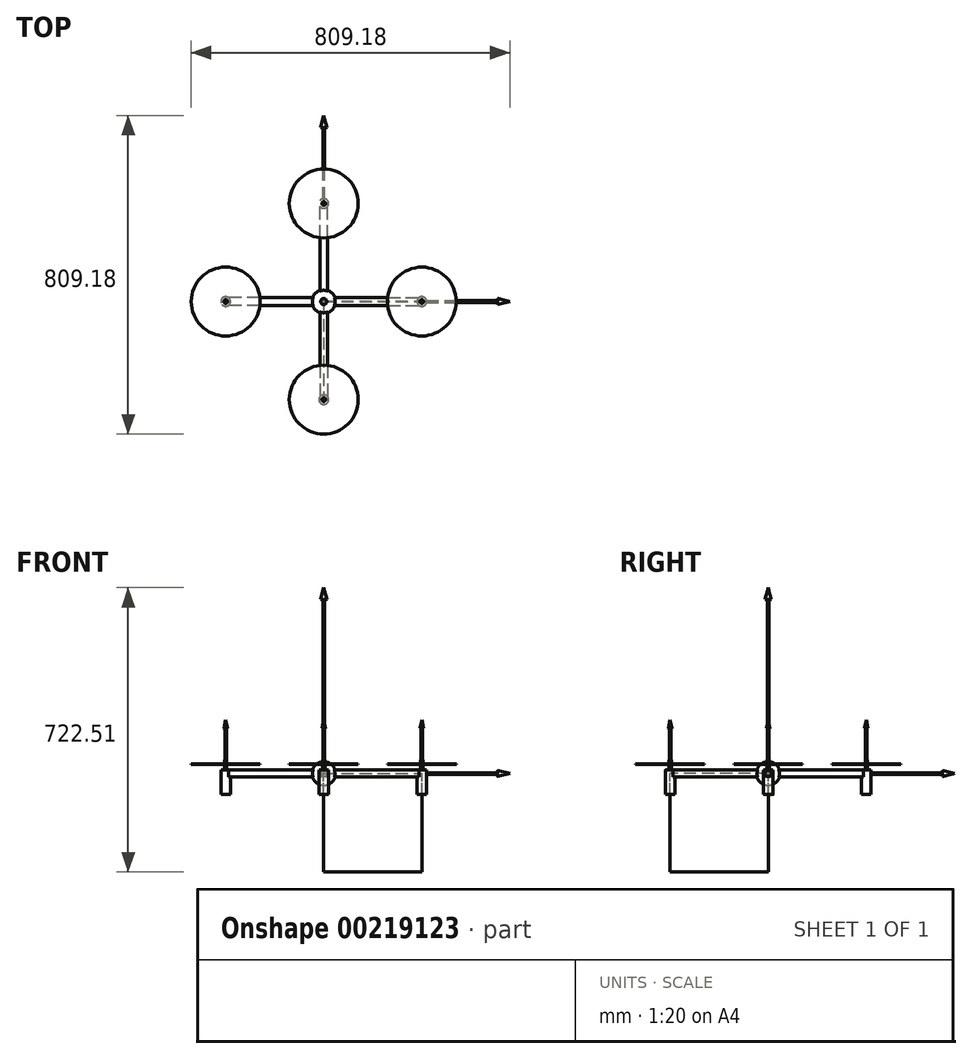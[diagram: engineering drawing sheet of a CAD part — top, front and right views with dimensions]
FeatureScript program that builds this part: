
annotation { "Feature Type Name" : "Feature", "Feature Type Description" : "" }
export const myFeature = defineFeature(function(context is Context, id is Id, definition is map)
    precondition{}
    {
        {
            var Q0;
            Q0=qCreatedBy(makeId("Top.planeOp"),FACE);
            var sketch = newSketch(context, id + "F0", { "sketchPlane" : qUnion([Q0])});
            skLineSegment(sketch, "E0.bottom", {"start": v(0, 0) * mm, "end": v(-10, 0) * mm});
            skLineSegment(sketch, "E0.top", {"start": v(7.68, 250) * mm, "end": v(-10, 250) * mm});
            skLineSegment(sketch, "E0.right", {"start": v(-10, 0) * mm, "end": v(-10, 250) * mm});
            skLineSegment(sketch, "E1.MirrorCS", {"start": v(-7.68, 250) * mm, "end": v(10, 250) * mm});
            skLineSegment(sketch, "E2.MirrorCS", {"start": v(0, 0) * mm, "end": v(10, 0) * mm});
            skLineSegment(sketch, "E3.MirrorCS", {"start": v(10, 0) * mm, "end": v(10, 250) * mm});
            skLineSegment(sketch, "E4.1.0", {"start": v(0.03, 10) * mm, "end": v(-249.97, 10) * mm});
            skLineSegment(sketch, "E4.1.1", {"start": v(0.03, -10) * mm, "end": v(-249.97, -10) * mm});
            skLineSegment(sketch, "E4.1.2", {"start": v(0.03, 0) * mm, "end": v(0.03, 10) * mm});
            skLineSegment(sketch, "E4.1.3", {"start": v(-249.97, 7.68) * mm, "end": v(-249.97, -10) * mm});
            skLineSegment(sketch, "E4.1.4", {"start": v(-249.97, -7.68) * mm, "end": v(-249.97, 10) * mm});
            skLineSegment(sketch, "E4.1.5", {"start": v(0.03, 0) * mm, "end": v(0.03, -10) * mm});
            skLineSegment(sketch, "E4.2.0", {"start": v(-9.97, 0.03) * mm, "end": v(-9.97, -249.97) * mm});
            skLineSegment(sketch, "E4.2.1", {"start": v(10.03, 0.03) * mm, "end": v(10.03, -249.97) * mm});
            skLineSegment(sketch, "E4.2.2", {"start": v(0.03, 0.03) * mm, "end": v(-9.97, 0.03) * mm});
            skLineSegment(sketch, "E4.2.3", {"start": v(-7.65, -249.97) * mm, "end": v(10.03, -249.97) * mm});
            skLineSegment(sketch, "E4.2.4", {"start": v(7.71, -249.97) * mm, "end": v(-9.97, -249.97) * mm});
            skLineSegment(sketch, "E4.2.5", {"start": v(0.03, 0.03) * mm, "end": v(10.03, 0.03) * mm});
            skLineSegment(sketch, "E4.3.0", {"start": v(0, -9.97) * mm, "end": v(250, -9.97) * mm});
            skLineSegment(sketch, "E4.3.1", {"start": v(0, 10.03) * mm, "end": v(250, 10.03) * mm});
            skLineSegment(sketch, "E4.3.2", {"start": v(0, 0.03) * mm, "end": v(0, -9.97) * mm});
            skLineSegment(sketch, "E4.3.3", {"start": v(250, -7.65) * mm, "end": v(250, 10.03) * mm});
            skLineSegment(sketch, "E4.3.4", {"start": v(250, 7.71) * mm, "end": v(250, -9.97) * mm});
            skLineSegment(sketch, "E4.3.5", {"start": v(0, 0.03) * mm, "end": v(0, 10.03) * mm});
            skPoint(sketch, "E4.center", {"position": v(0.01, 0.01) * mm});
            skCircle(sketch, "E5", {"center": v(0, 250) * mm, "radius": 10.03 * mm});
            skPoint(sketch, "E5.centerSnap0", {"position": v(1.16, 250) * mm});
            skSolve(sketch);
        }
        {
            var Q0;
            Q0 = qSketchRegion(id + "F0", true);
            extrude(context, id + "F1", {"entities" : qUnion([Q0]), "endBound" : BoundingType.SYMMETRIC, "depth" : 18 * mm});
        }
        {
            var Q0;
            Q0=qCreatedBy(makeId("Top.planeOp"),FACE);
            var sketch = newSketch(context, id + "F2", { "sketchPlane" : qUnion([Q0])});
            skArc(sketch, "E6", {"start": v(30, 0) * mm, "mid": v(0, 30) * mm, "end": v(-30, 0) * mm});
            skLineSegment(sketch, "E7", {"start": v(0, 0) * mm, "end": v(309.13, 0) * mm, "construction": true});
            skLineSegment(sketch, "E8", {"start": v(0, 0) * mm, "end": v(30, 0) * mm});
            skLineSegment(sketch, "E9", {"start": v(-30, 0) * mm, "end": v(0, 0) * mm});
            skLineSegment(sketch, "E10", {"start": v(0, 320.77) * mm, "end": v(0, 0) * mm, "construction": true});
            skSolve(sketch);
        }
        {
            var Q0;
            Q0=makeQuery(id+"F2.imprint","IMPRINT",FACE,{"disambiguationData":[TD([[makeQuery(id+"F2.imprint","IMPRINT",EDGE,{"derivedFrom":sQuery(id+"F2.wireOp",EDGE,"E6")}),1.0]])]});
            var Q1;
            Q1=sQuery(id+"F2.wireOp",EDGE,"E7");
            revolve(context, id + "F3", {"operationType" : NewBodyOperationType.ADD, "entities" : qUnion([Q0]), "axis" : qUnion([Q1]), "revolveType" : RevolveType.FULL});
        }
        {
            var Q0;
            Q0=makeQuery(id+"F1.opExtrude","CAP_FACE",FACE,{"disambiguationData":[OSD([sQuery(id+"F0.wireOp",EDGE,"E0.bottom"),sQuery(id+"F0.wireOp",EDGE,"E0.right"),sQuery(id+"F0.wireOp",EDGE,"E2.MirrorCS"),sQuery(id+"F0.wireOp",EDGE,"E3.MirrorCS"),sQuery(id+"F0.wireOp",EDGE,"E4.1.0"),sQuery(id+"F0.wireOp",EDGE,"E4.1.1"),sQuery(id+"F0.wireOp",EDGE,"E4.1.2"),sQuery(id+"F0.wireOp",EDGE,"E4.1.3"),sQuery(id+"F0.wireOp",EDGE,"E4.1.4"),sQuery(id+"F0.wireOp",EDGE,"E4.1.5"),sQuery(id+"F0.wireOp",EDGE,"E4.2.0"),sQuery(id+"F0.wireOp",EDGE,"E4.2.1"),sQuery(id+"F0.wireOp",EDGE,"E4.2.2"),sQuery(id+"F0.wireOp",EDGE,"E4.2.3"),sQuery(id+"F0.wireOp",EDGE,"E4.2.4"),sQuery(id+"F0.wireOp",EDGE,"E4.2.5"),sQuery(id+"F0.wireOp",EDGE,"E4.3.0"),sQuery(id+"F0.wireOp",EDGE,"E4.3.1"),sQuery(id+"F0.wireOp",EDGE,"E4.3.2"),sQuery(id+"F0.wireOp",EDGE,"E4.3.3"),sQuery(id+"F0.wireOp",EDGE,"E4.3.4"),sQuery(id+"F0.wireOp",EDGE,"E4.3.5"),sQuery(id+"F0.wireOp",EDGE,"E5")])],"isStart":false});
            var sketch = newSketch(context, id + "F4", { "sketchPlane" : qUnion([Q0])});
            skCircle(sketch, "E11", {"center": v(0, 249.17) * mm, "radius": 12.17 * mm});
            skCircle(sketch, "E12.1.0", {"center": v(-249.17, 0) * mm, "radius": 12.17 * mm});
            skCircle(sketch, "E12.2.0", {"center": v(0, -249.17) * mm, "radius": 12.17 * mm});
            skCircle(sketch, "E12.3.0", {"center": v(249.17, 0) * mm, "radius": 12.17 * mm});
            skPoint(sketch, "E12.center", {"position": v(0, 0) * mm});
            skSolve(sketch);
        }
        {
            var Q0;
            Q0 = qSketchRegion(id + "F4", true);
            extrude(context, id + "F5", {"entities" : qUnion([Q0]), "operationType" : NewBodyOperationType.ADD, "oppositeDirection" : true, "depth" : 62.5 * mm});
        }
        {
            var Q0;
            Q0=qCreatedBy(makeId("Front.planeOp"),FACE);
            var sketch = newSketch(context, id + "F6", { "sketchPlane" : qUnion([Q0])});
            skLineSegment(sketch, "E13", {"start": v(0, 0) * mm, "end": v(0, 184.57) * mm, "construction": true});
            skSolve(sketch);
        }
        {
            var Q0;
            Q0=qCreatedBy(makeId("Top.planeOp"),FACE);
            var sketch = newSketch(context, id + "F7", { "sketchPlane" : qUnion([Q0])});
            skLineSegment(sketch, "E14.0", {"start": v(-2, 441.97) * mm, "end": v(-2, 0) * mm});
            skLineSegment(sketch, "E15", {"start": v(0, 441.97) * mm, "end": v(0, 0) * mm});
            skLineSegment(sketch, "E16", {"start": v(0, 0) * mm, "end": v(-2, 0) * mm});
            skPoint(sketch, "E17.center", {"position": v(0, 0) * mm});
            skLineSegment(sketch, "E18", {"start": v(-2, 0) * mm, "end": v(0, 0) * mm});
            skLineSegment(sketch, "E19.1.0", {"start": v(441.97, 2) * mm, "end": v(441.97, 0) * mm});
            skLineSegment(sketch, "E19.1.1", {"start": v(441.97, 2) * mm, "end": v(0, 2) * mm});
            skLineSegment(sketch, "E19.1.2", {"start": v(441.97, 0) * mm, "end": v(0, 0) * mm});
            skLineSegment(sketch, "E19.1.3", {"start": v(0, 2) * mm, "end": v(0, 0) * mm});
            skLineSegment(sketch, "E20", {"start": v(-2, 441.97) * mm, "end": v(-7.85, 441.97) * mm});
            skLineSegment(sketch, "E21", {"start": v(0, 472.51) * mm, "end": v(-7.85, 441.97) * mm});
            skLineSegment(sketch, "E22", {"start": v(0, 472.51) * mm, "end": v(0, 441.97) * mm});
            skSolve(sketch);
        }
        {
            var Q0;
            Q0=makeQuery(id+"F7.imprint","IMPRINT",FACE,{"disambiguationData":[TD([[makeQuery(id+"F7.imprint","IMPRINT",EDGE,{"derivedFrom":sQuery(id+"F7.wireOp",EDGE,"E15")}),-1.0]])]});
            var Q1;
            {var subQ3=sQuery(id+"F7.wireOp",EDGE,"E21");Q1=makeQuery(id+"F7.imprint","IMPRINT",FACE,{"disambiguationData":[TD([[makeQuery(id+"F7.imprint","IMPRINT",EDGE,{"derivedFrom":subQ3}),-1.0]])]});}
            var Q2;
            Q2=sQuery(id+"F7.wireOp",EDGE,"E15");
            revolve(context, id + "F8", {"entities" : qUnion([Q0, Q1]), "axis" : qUnion([Q2]), "revolveType" : RevolveType.FULL});
        }
        {
            var Q0;
            Q0=makeQuery(id+"F8.opRevolve","SWEPT_BODY",BODY,{"disambiguationData":[OSD([sQuery(id+"F7.wireOp",EDGE,"E15"),sQuery(id+"F7.wireOp",EDGE,"E14.0"),sQuery(id+"F7.wireOp",EDGE,"phnClhmD-Ye00-Ug2d-337D-V6CSu4RFdTta"),sQuery(id+"F7.wireOp",EDGE,"E18")])]});
            var Q1;
            Q1=sQuery(id+"F2.wireOp",EDGE,"E8");
            circularPattern(context, id + "F9", {"entities" : qUnion([Q0]), "axis" : qUnion([Q1]), "angle" : 90 * degree, "instanceCount" : 2, "equalSpace" : true});
        }
        {
            var Q0;
            Q0=makeQuery(id+"F9.opPattern","COPY",BODY,{"derivedFrom":makeQuery(id+"F8.opRevolve","SWEPT_BODY",BODY,{"disambiguationData":[OSD([sQuery(id+"F7.wireOp",EDGE,"E15"),sQuery(id+"F7.wireOp",EDGE,"E14.0"),sQuery(id+"F7.wireOp",EDGE,"phnClhmD-Ye00-Ug2d-337D-V6CSu4RFdTta"),sQuery(id+"F7.wireOp",EDGE,"E18"),sQuery(id+"F7.wireOp",EDGE,"E19.1.3")])]}),"instanceName":"1"});
            var Q1;
            Q1=sQuery(id+"F2.wireOp",EDGE,"E10");
            circularPattern(context, id + "F10", {"operationType" : NewBodyOperationType.ADD, "entities" : qUnion([Q0]), "axis" : qUnion([Q1]), "angle" : 270 * degree, "instanceCount" : 2, "equalSpace" : true});
        }
        {
            var Q0;
            {var subQ0=sQuery(id+"F0.wireOp",EDGE,"E0.right");var subQ1=sQuery(id+"F0.wireOp",EDGE,"E4.3.1");var subQ2=sQuery(id+"F0.wireOp",EDGE,"E3.MirrorCS");var subQ3=sQuery(id+"F0.wireOp",EDGE,"E5");Q0=makeQuery(id+"F5.boolean.opBoolean","MERGE",FACE,{"derivedFrom":[makeQuery(id+"F3.boolean.opBoolean","SPLIT",FACE,{"disambiguationData":[TD([makeQuery(id+"F1.opExtrude","SWEPT_FACE",FACE,{"disambiguationData":[OSD([subQ0])]})])],"derivedFrom":makeQuery(id+"F1.opExtrude","CAP_FACE",FACE,{"disambiguationData":[OSD([sQuery(id+"F0.wireOp",EDGE,"E0.bottom"),subQ0,sQuery(id+"F0.wireOp",EDGE,"E2.MirrorCS"),subQ2,sQuery(id+"F0.wireOp",EDGE,"E4.1.0"),sQuery(id+"F0.wireOp",EDGE,"E4.1.1"),sQuery(id+"F0.wireOp",EDGE,"E4.1.2"),sQuery(id+"F0.wireOp",EDGE,"E4.1.3"),sQuery(id+"F0.wireOp",EDGE,"E4.1.4"),sQuery(id+"F0.wireOp",EDGE,"E4.1.5"),sQuery(id+"F0.wireOp",EDGE,"E4.2.0"),sQuery(id+"F0.wireOp",EDGE,"E4.2.1"),sQuery(id+"F0.wireOp",EDGE,"E4.2.2"),sQuery(id+"F0.wireOp",EDGE,"E4.2.3"),sQuery(id+"F0.wireOp",EDGE,"E4.2.4"),sQuery(id+"F0.wireOp",EDGE,"E4.2.5"),sQuery(id+"F0.wireOp",EDGE,"E4.3.0"),subQ1,sQuery(id+"F0.wireOp",EDGE,"E4.3.2"),sQuery(id+"F0.wireOp",EDGE,"E4.3.3"),sQuery(id+"F0.wireOp",EDGE,"E4.3.4"),sQuery(id+"F0.wireOp",EDGE,"E4.3.5"),subQ3])],"isStart":false})}),makeQuery(id+"F5.opExtrude","CAP_FACE",FACE,{"disambiguationData":[OSD([sQuery(id+"F4.wireOp",EDGE,"E11")])],"isStart":true})]});}
            var sketch = newSketch(context, id + "F11", { "sketchPlane" : qUnion([Q0])});
            skPoint(sketch, "E23", {"position": v(0, 249.17) * mm});
            skCircle(sketch, "E24", {"center": v(0, 249.17) * mm, "radius": 2.79 * mm});
            skCircle(sketch, "E25.1.0", {"center": v(-249.17, 0) * mm, "radius": 2.79 * mm});
            skCircle(sketch, "E25.2.0", {"center": v(0, -249.17) * mm, "radius": 2.79 * mm});
            skCircle(sketch, "E25.3.0", {"center": v(249.17, 0) * mm, "radius": 2.79 * mm});
            skPoint(sketch, "E25.center", {"position": v(0, 0) * mm});
            skSolve(sketch);
        }
        {
            var Q0;
            Q0 = qSketchRegion(id + "F11", true);
            extrude(context, id + "F12", {"entities" : qUnion([Q0]), "operationType" : NewBodyOperationType.ADD, "depth" : 25 * mm});
        }
        {
            var Q0;
            Q0=qCreatedBy(makeId("Top.planeOp"),FACE);
            cPlane(context, id + "F13", {"entities" : qUnion([Q0]), "cplaneType" : CPlaneType.OFFSET, "offset" : 25 * mm, "width" : 150 * mm, "height" : 150 * mm});
        }
        {
            var Q0;
            Q0=qCreatedBy(id+"F13.planeOp",FACE);
            var sketch = newSketch(context, id + "F14", { "sketchPlane" : qUnion([Q0])});
            skCircle(sketch, "E26", {"center": v(0, 249.17) * mm, "radius": 87.5 * mm});
            skSolve(sketch);
        }
        {
            var Q0;
            Q0 = qSketchRegion(id + "F14", true);
            extrude(context, id + "F15", {"entities" : qUnion([Q0]), "oppositeDirection" : true, "depth" : 2 * mm});
        }
        {
            var Q0;
            Q0=sQuery(id+"F11.wireOp",VERTEX,"E23");
            var Q1;
            Q1=makeQuery(id+"F15.opExtrude","SWEPT_BODY",BODY,{"disambiguationData":[OSD([sQuery(id+"F14.wireOp",EDGE,"E26")])]});
            hole(context, id + "F16", {"style" : HoleStyle.SIMPLE, "endStyle" : HoleEndStyle.THROUGH, "oppositeDirection" : true, "holeDiameter" : 5 * mm, "locations" : qUnion([Q0]), "scope" : qUnion([Q1]), "isTappedThrough" : true});
        }
        {
            var Q0;
            Q0=makeQuery(id+"F15.opExtrude","SWEPT_BODY",BODY,{"disambiguationData":[OSD([sQuery(id+"F14.wireOp",EDGE,"E26")])]});
            var Q1;
            Q1=makeQuery(id+"F9.opPattern","COPY",EDGE,{"derivedFrom":makeQuery(id+"F8.opRevolve","SWEPT_EDGE",EDGE,{"disambiguationData":[OSD([sQuery(id+"F7.wireOp",EDGE,"E20"),sQuery(id+"F7.wireOp",EDGE,"E21")])]}),"instanceName":"1"});
            circularPattern(context, id + "F17", {"operationType" : NewBodyOperationType.ADD, "entities" : qUnion([Q0]), "axis" : qUnion([Q1]), "angle" : 360 * degree, "instanceCount" : 4, "equalSpace" : true});
        }
        {
            var Q0;
            Q0=makeQuery(id+"F12.opExtrude","CAP_FACE",FACE,{"disambiguationData":[OSD([sQuery(id+"F11.wireOp",EDGE,"E24")])],"isStart":false});
            var sketch = newSketch(context, id + "F18", { "sketchPlane" : qUnion([Q0])});
            skCircle(sketch, "E27", {"center": v(0, 249.17) * mm, "radius": 2.05 * mm});
            skSolve(sketch);
        }
        {
            var Q0;
            Q0 = qSketchRegion(id + "F18", true);
            extrude(context, id + "F19", {"entities" : qUnion([Q0]), "depth" : 80 * mm});
        }
        {
            var Q0;
            Q0=sQuery(id+"F2.wireOp",EDGE,"E10");
            var Q1;
            Q1=sQuery(id+"F11.wireOp",VERTEX,"E23");
            cPlane(context, id + "F20", {"entities" : qUnion([Q0, Q1]), "cplaneType" : CPlaneType.LINE_POINT, "offset" : 100 * mm, "oppositeDirection" : true, "width" : 150 * mm, "height" : 150 * mm});
        }
        {
            var Q0;
            Q0=qCreatedBy(id+"F20.planeOp",FACE);
            var sketch = newSketch(context, id + "F21", { "sketchPlane" : qUnion([Q0])});
            skLineSegment(sketch, "E28", {"start": v(0, 135.8) * mm, "end": v(4.68, 114) * mm});
            skLineSegment(sketch, "E29", {"start": v(4.68, 114) * mm, "end": v(0, 114) * mm});
            skLineSegment(sketch, "E30", {"start": v(0, 114) * mm, "end": v(0, 135.8) * mm});
            skSolve(sketch);
        }
        {
            var Q0;
            Q0 = qSketchRegion(id + "F21", true);
            var Q1;
            Q1=sQuery(id+"F21.wireOp",EDGE,"E30");
            revolve(context, id + "F22", {"operationType" : NewBodyOperationType.ADD, "entities" : qUnion([Q0]), "axis" : qUnion([Q1]), "revolveType" : RevolveType.FULL});
        }
        {
            var Q0;
            Q0=makeQuery(id+"F19.opExtrude","SWEPT_BODY",BODY,{"disambiguationData":[OSD([sQuery(id+"F18.wireOp",EDGE,"E27")])]});
            var Q1;
            Q1=makeQuery(id+"F9.opPattern","COPY",FACE,{"derivedFrom":makeQuery(id+"F8.opRevolve","SWEPT_FACE",FACE,{"disambiguationData":[OSD([sQuery(id+"F7.wireOp",EDGE,"E14.0")])]}),"instanceName":"1"});
            circularPattern(context, id + "F23", {"operationType" : NewBodyOperationType.ADD, "entities" : qUnion([Q0]), "axis" : qUnion([Q1]), "angle" : 360 * degree, "instanceCount" : 4, "equalSpace" : true});
        }
        {
            var Q0;
            Q0=qCreatedBy(makeId("Top.planeOp"),FACE);
            var sketch = newSketch(context, id + "F24", { "sketchPlane" : qUnion([Q0])});
            skLineSegment(sketch, "E31", {"start": v(0, 0) * mm, "end": v(0, -249.17) * mm});
            skLineSegment(sketch, "E32", {"start": v(0, 0) * mm, "end": v(249.17, 0) * mm});
            skLineSegment(sketch, "E33.0", {"start": v(-1, 1) * mm, "end": v(-1, -249.17) * mm});
            skLineSegment(sketch, "E33.1", {"start": v(-1, 1) * mm, "end": v(249.17, 1) * mm});
            skLineSegment(sketch, "E34", {"start": v(-1, -249.17) * mm, "end": v(0, -249.17) * mm});
            skLineSegment(sketch, "E35", {"start": v(249.17, 1) * mm, "end": v(249.17, 0) * mm});
            skSolve(sketch);
        }
        {
            var Q0;
            Q0 = qSketchRegion(id + "F24", true);
            var Q1;
            Q1=sQuery(id+"F24.wireOp",EDGE,"E31");
            var Q2;
            Q2=sQuery(id+"F24.wireOp",EDGE,"E32");
            extrude(context, id + "F25", {"entities" : qUnion([Q0]), "surfaceEntities" : qUnion([Q1, Q2]), "oppositeDirection" : true, "depth" : 250 * mm});
        }
    });
